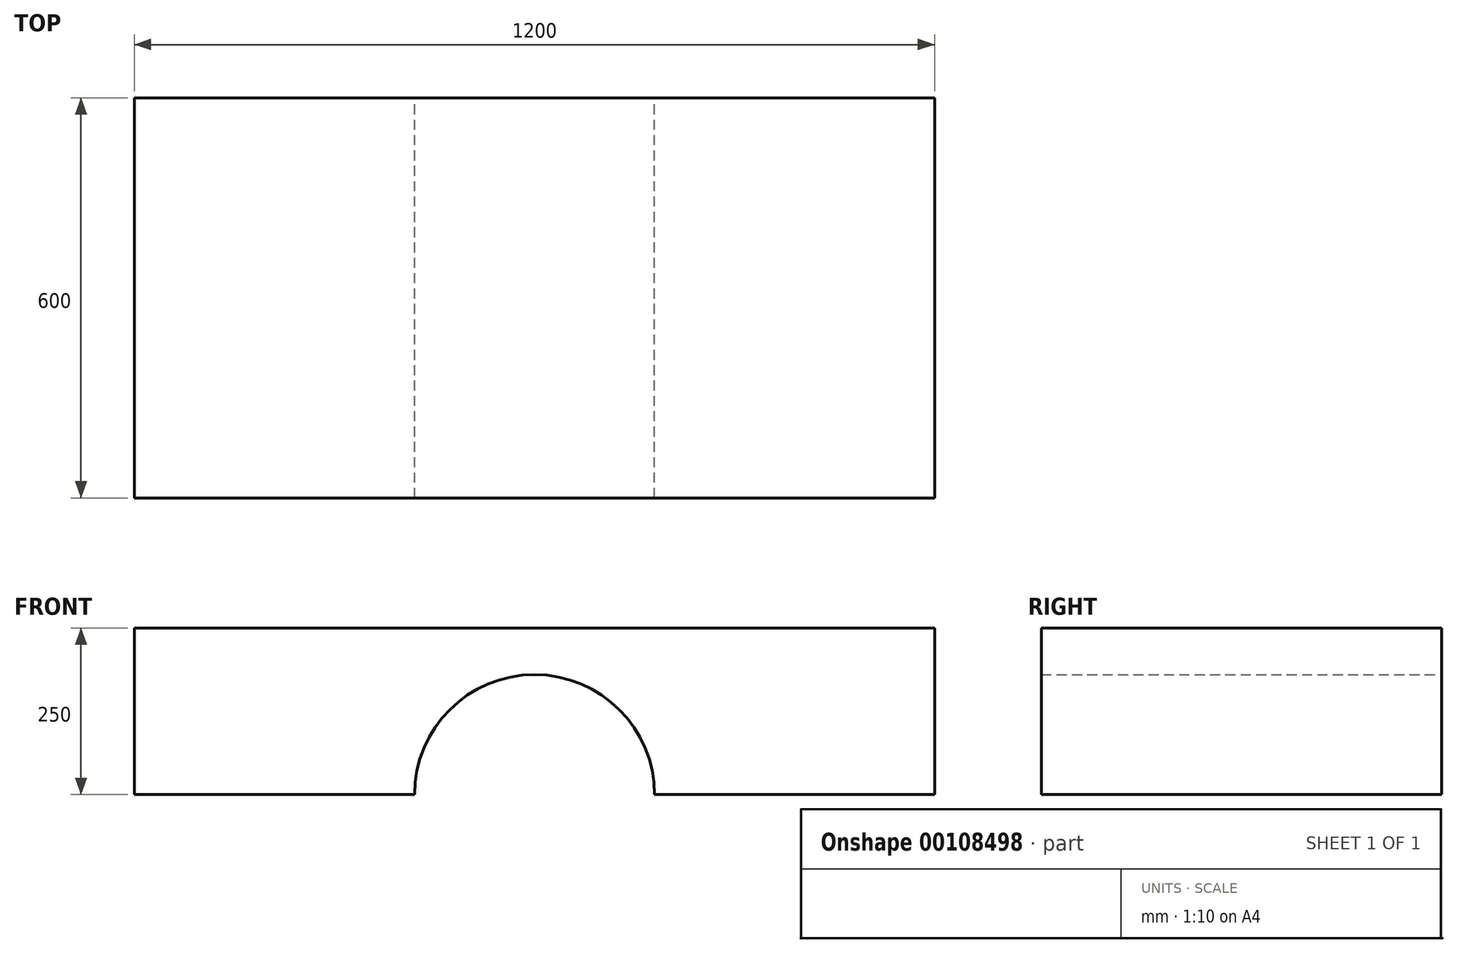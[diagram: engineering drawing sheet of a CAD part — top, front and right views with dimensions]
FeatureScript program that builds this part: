
annotation { "Feature Type Name" : "Feature", "Feature Type Description" : "" }
export const myFeature = defineFeature(function(context is Context, id is Id, definition is map)
    precondition{}
    {
        {
            var Q0;
            Q0=qCreatedBy(makeId("Front.planeOp"),FACE);
            var sketch = newSketch(context, id + "F0", { "sketchPlane" : qUnion([Q0])});
            skLineSegment(sketch, "E0.bottom", {"start": v(-600, -125) * mm, "end": v(-180, -125) * mm});
            skLineSegment(sketch, "E0.top", {"start": v(-600, 125) * mm, "end": v(600, 125) * mm});
            skLineSegment(sketch, "E0.left", {"start": v(-600, -125) * mm, "end": v(-600, 125) * mm});
            skLineSegment(sketch, "E0.right", {"start": v(600, -125) * mm, "end": v(600, 125) * mm});
            skPoint(sketch, "E0.middle", {"position": v(0, 0) * mm});
            skArc(sketch, "E1", {"start": v(180, -125) * mm, "mid": v(0, 55) * mm, "end": v(-180, -125) * mm});
            skLineSegment(sketch, "E2.trimOffspring", {"start": v(180, -125) * mm, "end": v(600, -125) * mm});
            skSolve(sketch);
        }
        {
            var Q0;
            Q0 = qSketchRegion(id + "F0", true);
            extrude(context, id + "F1", {"entities" : qUnion([Q0]), "depth" : 600 * mm});
        }
    });
